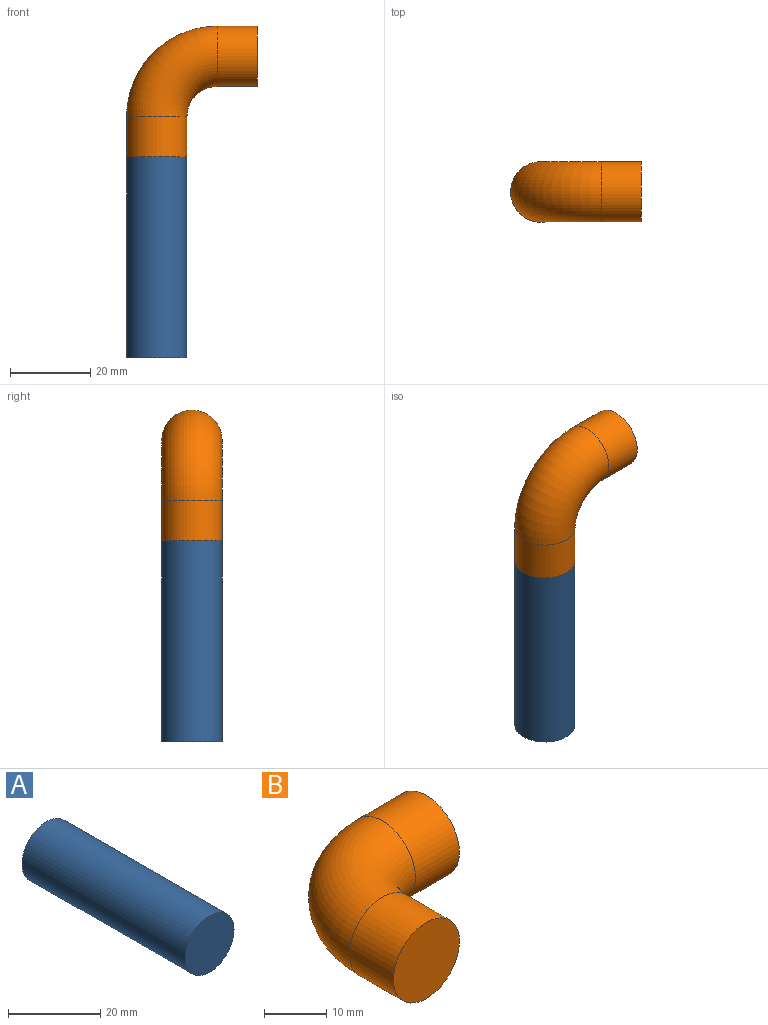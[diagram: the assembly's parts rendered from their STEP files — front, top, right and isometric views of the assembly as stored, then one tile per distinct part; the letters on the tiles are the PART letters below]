
ASSEMBLY  parts=2 mates=1
PART A: 3 faces, bbox 15x50x15 mm
  f0: cylinder r=7.5mm len=50mm, axis (0,1,0), area 2356.2mm2, adj f1,f2
  f1: plane 15x15mm, normal (0,-1,0), area 176.7mm2, adj f0
  f2: plane 15x15mm, normal (0,1,0), area 176.7mm2, adj f0
PART B: 5 faces, bbox 34.4x34.4x15 mm
  f0: plane 15x15mm, normal (0,-1,0), area 176.7mm2, adj f2
  f1: plane 15x15mm, normal (1,0,0), area 176.7mm2, adj f4
  f2: cylinder r=7.5mm len=15mm, axis (0,1,0), area 471.2mm2, adj f0,f3
  f3: torus R=15mm, axis (0,0,-1), area 1110.3mm2, adj f2,f4
  f4: cylinder r=7.5mm len=15mm, axis (1,0,0), area 471.2mm2, adj f1,f3
PLACE A rot(axis=(-1,0,0),90deg) t=(7020,4110,0)mm
PLACE B rot(axis=(-0.58,0.58,0.58),120deg) t=(7045,4110,75)mm
MATE revolute B.f4 <-> A.f0  axis (0,0,-1) through (7020,4110,50)mm
